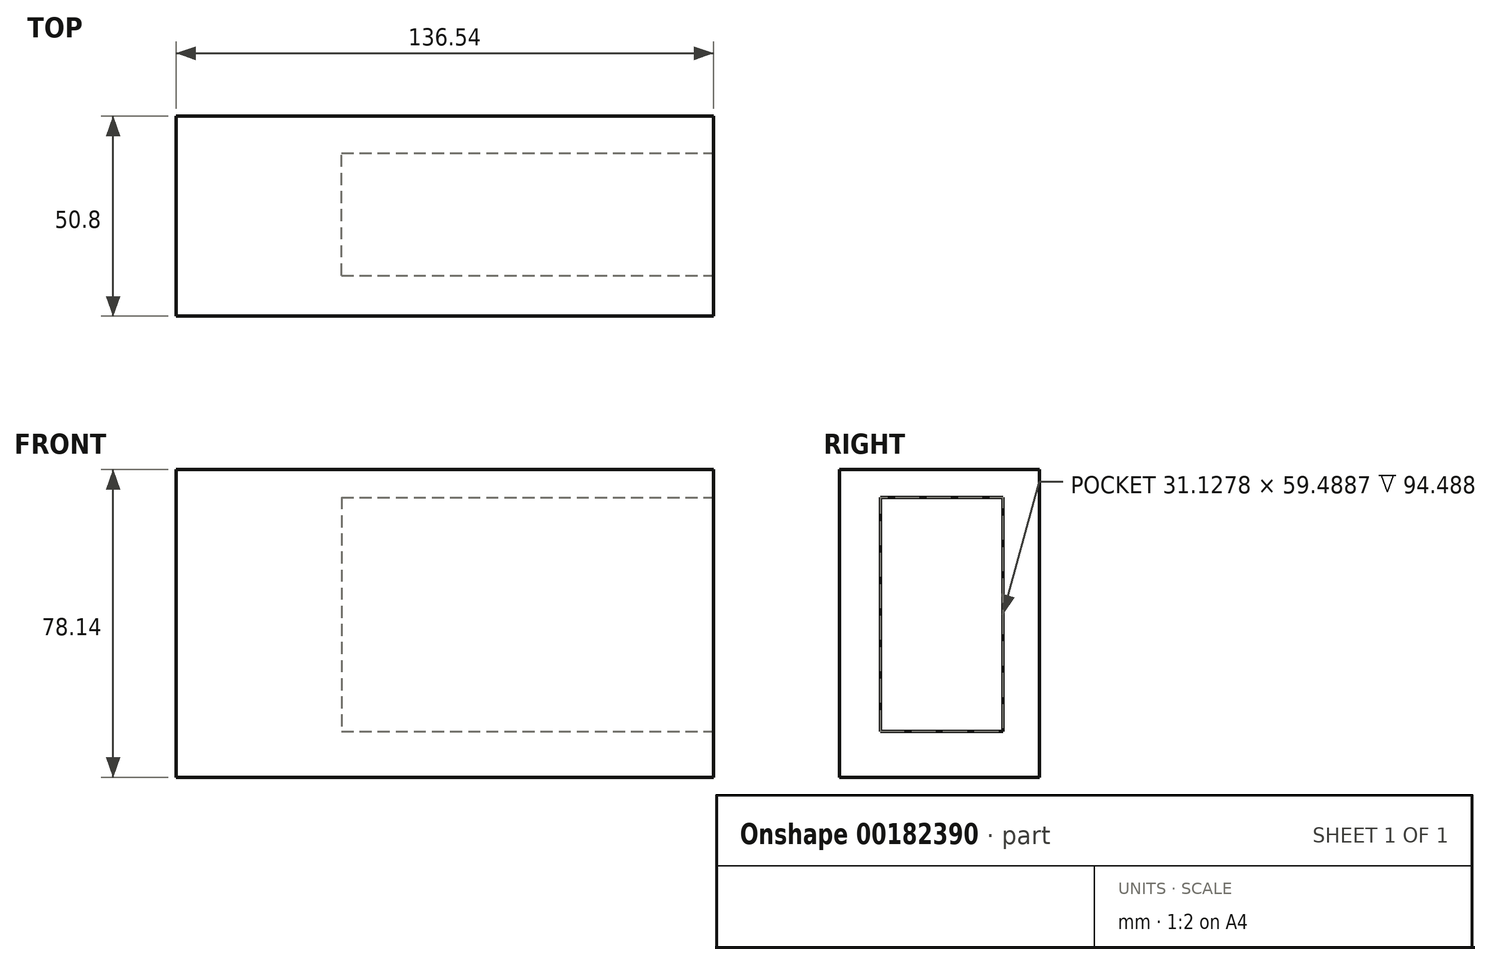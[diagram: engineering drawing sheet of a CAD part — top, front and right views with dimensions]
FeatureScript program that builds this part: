
annotation { "Feature Type Name" : "Feature", "Feature Type Description" : "" }
export const myFeature = defineFeature(function(context is Context, id is Id, definition is map)
    precondition{}
    {
        {
            var Q0;
            Q0=qCreatedBy(makeId("Front.planeOp"),FACE);
            var sketch = newSketch(context, id + "F0", { "sketchPlane" : qUnion([Q0])});
            skLineSegment(sketch, "E0.bottom", {"start": v(68.27, -39.07) * mm, "end": v(-68.27, -39.07) * mm});
            skLineSegment(sketch, "E0.top", {"start": v(68.27, 39.07) * mm, "end": v(-68.27, 39.07) * mm});
            skLineSegment(sketch, "E0.left", {"start": v(68.27, -39.07) * mm, "end": v(68.27, 39.07) * mm});
            skLineSegment(sketch, "E0.right", {"start": v(-68.27, -39.07) * mm, "end": v(-68.27, 39.07) * mm});
            skPoint(sketch, "E0.middle", {"position": v(0, 0) * mm});
            skSolve(sketch);
        }
        {
            var Q0;
            Q0=makeQuery(id+"F0.imprint","IMPRINT",FACE,{"disambiguationData":[TD([[makeQuery(id+"F0.imprint","IMPRINT",EDGE,{"derivedFrom":sQuery(id+"F0.wireOp",EDGE,"E0.bottom")}),-1.0]])]});
            extrude(context, id + "F1", {"entities" : qUnion([Q0]), "depth" : 50.8 * mm});
        }
        {
            var Q0;
            Q0=makeQuery(id+"F1.opExtrude","SWEPT_FACE",FACE,{"disambiguationData":[OSD([sQuery(id+"F0.wireOp",EDGE,"E0.left")])]});
            var sketch = newSketch(context, id + "F2", { "sketchPlane" : qUnion([Q0])});
            skLineSegment(sketch, "E1.bottom", {"start": v(-40.43, 32.05) * mm, "end": v(-9.3, 32.05) * mm});
            skLineSegment(sketch, "E1.top", {"start": v(-40.43, -27.44) * mm, "end": v(-9.3, -27.44) * mm});
            skLineSegment(sketch, "E1.left", {"start": v(-40.43, 32.05) * mm, "end": v(-40.43, -27.44) * mm});
            skLineSegment(sketch, "E1.right", {"start": v(-9.3, 32.05) * mm, "end": v(-9.3, -27.44) * mm});
            skSolve(sketch);
        }
        {
            var Q0;
            Q0=makeQuery(id+"F2.imprint","IMPRINT",FACE,{"disambiguationData":[TD([[makeQuery(id+"F2.imprint","IMPRINT",EDGE,{"derivedFrom":sQuery(id+"F2.wireOp",EDGE,"E1.bottom")}),-1.0]])]});
            extrude(context, id + "F3", {"entities" : qUnion([Q0]), "operationType" : NewBodyOperationType.REMOVE, "oppositeDirection" : true, "depth" : 94.49 * mm});
        }
    });
